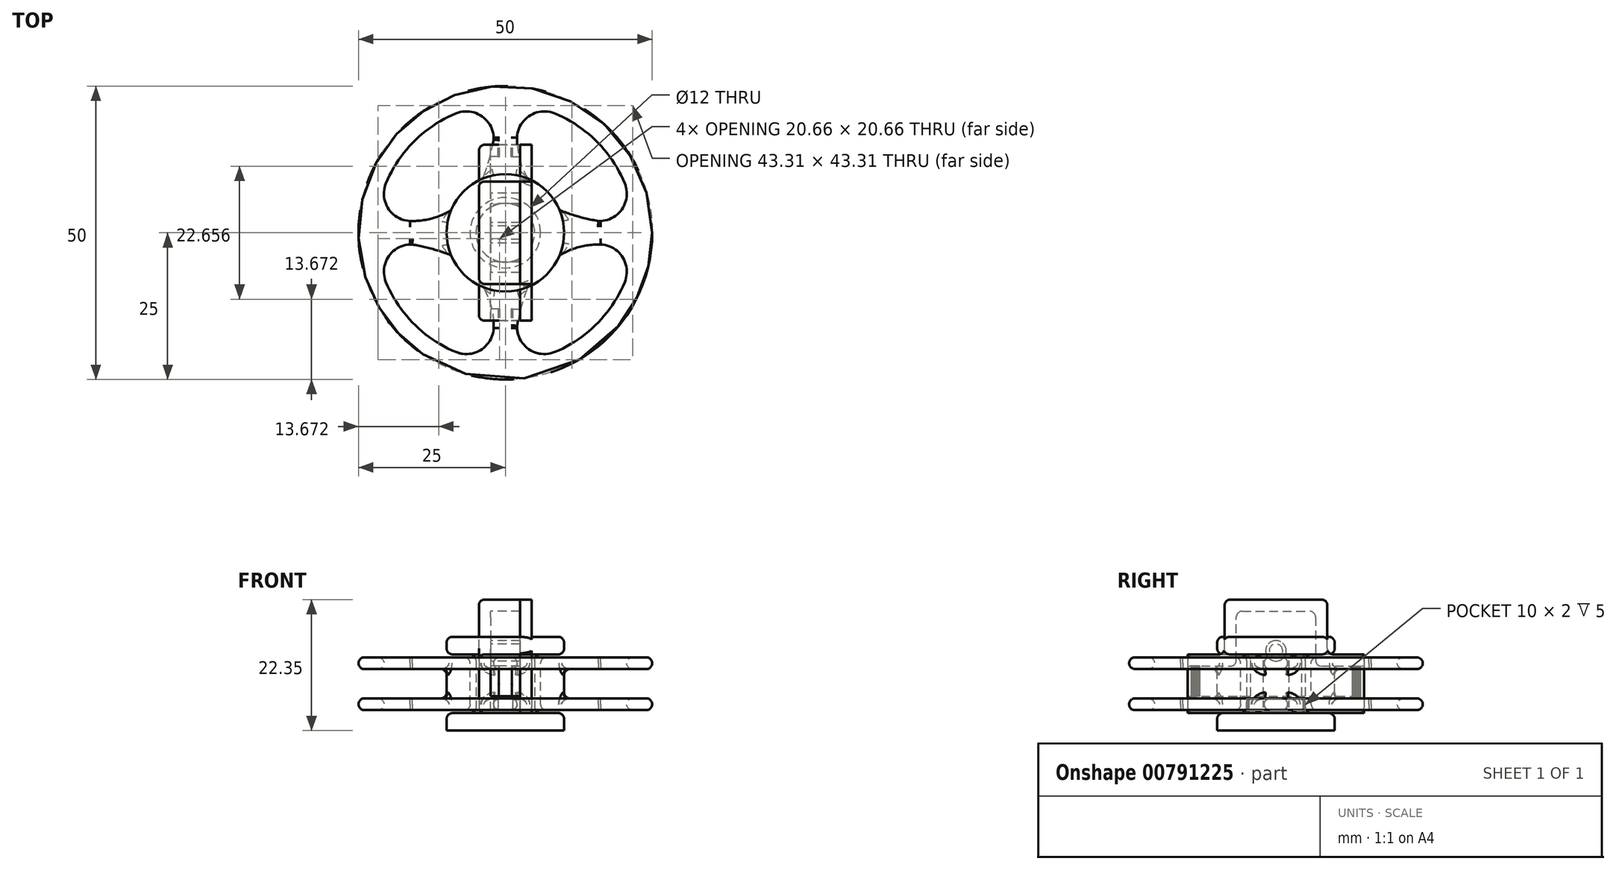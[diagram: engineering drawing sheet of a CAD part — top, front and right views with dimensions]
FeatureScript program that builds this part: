
annotation { "Feature Type Name" : "Feature", "Feature Type Description" : "" }
export const myFeature = defineFeature(function(context is Context, id is Id, definition is map)
    precondition{}
    {
        {
            var Q0;
            Q0=qCreatedBy(makeId("Right.planeOp"),FACE);
            var sketch = newSketch(context, id + "F0", { "sketchPlane" : qUnion([Q0])});
            skPoint(sketch, "E0.middle", {"position": v(0, 0) * mm});
            skLineSegment(sketch, "E1.top", {"start": v(0, 4.5) * mm, "end": v(25, 4.5) * mm});
            skLineSegment(sketch, "E1.right", {"start": v(25, 2.5) * mm, "end": v(25, 4.5) * mm});
            skLineSegment(sketch, "E2.top", {"start": v(0, -4.5) * mm, "end": v(25, -4.5) * mm});
            skLineSegment(sketch, "E2.right", {"start": v(25, -2.5) * mm, "end": v(25, -4.5) * mm});
            skLineSegment(sketch, "E3", {"start": v(10, 2.5) * mm, "end": v(25, 2.5) * mm});
            skLineSegment(sketch, "E4", {"start": v(10, -2.5) * mm, "end": v(25, -2.5) * mm});
            skLineSegment(sketch, "E5", {"start": v(0, 4.5) * mm, "end": v(0, -4.5) * mm});
            skLineSegment(sketch, "E6", {"start": v(10, 2.5) * mm, "end": v(10, -2.5) * mm});
            skSolve(sketch);
        }
        {
            var Q0;
            Q0=makeQuery(id+"F0.imprint","IMPRINT",FACE,{"disambiguationData":[TD([[makeQuery(id+"F0.imprint","IMPRINT",EDGE,{"derivedFrom":sQuery(id+"F0.wireOp",EDGE,"E1.top")}),-1.0]])]});
            var Q1;
            Q1=sQuery(id+"F0.wireOp",EDGE,"E5");
            revolve(context, id + "F1", {"surfaceOperationType" : NewSurfaceOperationType.NEW, "entities" : qUnion([Q0]), "axis" : qUnion([Q1]), "revolveType" : RevolveType.FULL});
        }
        {
            var Q0;
            Q0=makeQuery(id+"F1.opRevolve","SWEPT_FACE",FACE,{"disambiguationData":[OSD([sQuery(id+"F0.wireOp",EDGE,"E1.top")])]});
            var sketch = newSketch(context, id + "F2", { "sketchPlane" : qUnion([Q0])});
            skCircle(sketch, "E7", {"center": v(0, 0) * mm, "radius": 6 * mm});
            skCircle(sketch, "E8", {"center": v(0, 0) * mm, "radius": 10 * mm});
            skCircle(sketch, "E9", {"center": v(0, 0) * mm, "radius": 22 * mm});
            skLineSegment(sketch, "E10", {"start": v(-2, 9.8) * mm, "end": v(-2, 21.9) * mm});
            skLineSegment(sketch, "E11", {"start": v(2, 9.8) * mm, "end": v(2, 21.9) * mm});
            skLineSegment(sketch, "E12.1.0", {"start": v(-9.8, -2) * mm, "end": v(-21.9, -2) * mm});
            skLineSegment(sketch, "E12.1.1", {"start": v(-9.8, 2) * mm, "end": v(-21.9, 2) * mm});
            skLineSegment(sketch, "E12.2.0", {"start": v(2, -9.8) * mm, "end": v(2, -21.9) * mm});
            skLineSegment(sketch, "E12.2.1", {"start": v(-2, -9.8) * mm, "end": v(-2, -21.9) * mm});
            skLineSegment(sketch, "E12.3.0", {"start": v(9.8, 2) * mm, "end": v(21.9, 2) * mm});
            skLineSegment(sketch, "E12.3.1", {"start": v(9.8, -2) * mm, "end": v(21.9, -2) * mm});
            skArc(sketch, "E13", {"start": v(-15.85, 2) * mm, "mid": v(-12.42, 2.47) * mm, "end": v(-9.24, 3.83) * mm});
            skArc(sketch, "E14", {"start": v(-3.83, 9.24) * mm, "mid": v(-2.74, 12.5) * mm, "end": v(-2, 15.85) * mm});
            skArc(sketch, "E15", {"start": v(-20.33, 8.42) * mm, "mid": v(-19.85, 3.99) * mm, "end": v(-15.85, 2) * mm});
            skArc(sketch, "E16", {"start": v(-2, 15.85) * mm, "mid": v(-3.99, 19.85) * mm, "end": v(-8.42, 20.33) * mm});
            skArc(sketch, "E17.1.0", {"start": v(-9.24, -3.83) * mm, "mid": v(-12.5, -2.74) * mm, "end": v(-15.85, -2) * mm});
            skArc(sketch, "E17.1.1", {"start": v(-15.85, -2) * mm, "mid": v(-19.85, -3.99) * mm, "end": v(-20.33, -8.42) * mm});
            skArc(sketch, "E17.1.2", {"start": v(-8.42, -20.33) * mm, "mid": v(-3.99, -19.85) * mm, "end": v(-2, -15.85) * mm});
            skArc(sketch, "E17.1.3", {"start": v(-2, -15.85) * mm, "mid": v(-2.47, -12.42) * mm, "end": v(-3.83, -9.24) * mm});
            skArc(sketch, "E17.2.0", {"start": v(3.83, -9.24) * mm, "mid": v(2.74, -12.5) * mm, "end": v(2, -15.85) * mm});
            skArc(sketch, "E17.2.1", {"start": v(2, -15.85) * mm, "mid": v(3.99, -19.85) * mm, "end": v(8.42, -20.33) * mm});
            skArc(sketch, "E17.2.2", {"start": v(20.33, -8.42) * mm, "mid": v(19.85, -3.99) * mm, "end": v(15.85, -2) * mm});
            skArc(sketch, "E17.2.3", {"start": v(15.85, -2) * mm, "mid": v(12.42, -2.47) * mm, "end": v(9.24, -3.83) * mm});
            skArc(sketch, "E17.3.0", {"start": v(9.24, 3.83) * mm, "mid": v(12.5, 2.74) * mm, "end": v(15.85, 2) * mm});
            skArc(sketch, "E17.3.1", {"start": v(15.85, 2) * mm, "mid": v(19.85, 3.99) * mm, "end": v(20.33, 8.42) * mm});
            skArc(sketch, "E17.3.2", {"start": v(8.42, 20.33) * mm, "mid": v(3.99, 19.85) * mm, "end": v(2, 15.85) * mm});
            skArc(sketch, "E17.3.3", {"start": v(2, 15.85) * mm, "mid": v(2.47, 12.42) * mm, "end": v(3.83, 9.24) * mm});
            skSolve(sketch);
        }
        {
            var Q0;
            {var subQ1=sQuery(id+"F2.wireOp",EDGE,"E13");Q0=makeQuery(id+"F2.imprint","IMPRINT",FACE,{"disambiguationData":[TD([[makeQuery(id+"F2.imprint","IMPRINT",EDGE,{"derivedFrom":subQ1}),1.0]])]});}
            var Q1;
            {var subQ8=sQuery(id+"F2.wireOp",EDGE,"E17.1.0");Q1=makeQuery(id+"F2.imprint","IMPRINT",FACE,{"disambiguationData":[TD([[makeQuery(id+"F2.imprint","IMPRINT",EDGE,{"derivedFrom":subQ8}),1.0]])]});}
            var Q2;
            {var subQ1=sQuery(id+"F2.wireOp",EDGE,"E17.2.0");Q2=makeQuery(id+"F2.imprint","IMPRINT",FACE,{"disambiguationData":[TD([[makeQuery(id+"F2.imprint","IMPRINT",EDGE,{"derivedFrom":subQ1}),1.0]])]});}
            var Q3;
            {var subQ5=sQuery(id+"F2.wireOp",EDGE,"E17.3.0");Q3=makeQuery(id+"F2.imprint","IMPRINT",FACE,{"disambiguationData":[TD([[makeQuery(id+"F2.imprint","IMPRINT",EDGE,{"derivedFrom":subQ5}),1.0]])]});}
            var Q4;
            Q4=makeQuery(id+"F2.imprint","IMPRINT",FACE,{"disambiguationData":[TD([[makeQuery(id+"F2.imprint","IMPRINT",EDGE,{"derivedFrom":sQuery(id+"F2.wireOp",EDGE,"E7")}),1.0]])]});
            extrude(context, id + "F3", {"entities" : qUnion([Q0, Q1, Q2, Q3, Q4]), "operationType" : NewBodyOperationType.REMOVE, "oppositeDirection" : true, "depth" : 25 * mm, "offsetDistance" : 25 * mm});
        }
        {
            var Q0;
            Q0=makeQuery(id+"F1.opRevolve","SWEPT_FACE",FACE,{"disambiguationData":[OSD([sQuery(id+"F0.wireOp",EDGE,"E1.top")])]});
            var Q1;
            Q1=makeQuery(id+"F1.opRevolve","SWEPT_FACE",FACE,{"disambiguationData":[OSD([sQuery(id+"F0.wireOp",EDGE,"E2.top")])]});
            var Q2;
            Q2=makeQuery(id+"F1.opRevolve","SWEPT_FACE",FACE,{"disambiguationData":[OSD([sQuery(id+"F0.wireOp",EDGE,"E3")])]});
            var Q3;
            Q3=makeQuery(id+"F1.opRevolve","SWEPT_FACE",FACE,{"disambiguationData":[OSD([sQuery(id+"F0.wireOp",EDGE,"E4")])]});
            var Q4;
            {var subQ0=sQuery(id+"F2.wireOp",EDGE,"E8");Q4=makeQuery(id+"F3.boolean.opBoolean","MERGE",FACE,{"derivedFrom":[makeQuery(id+"F1.opRevolve","SWEPT_FACE",FACE,{"disambiguationData":[OSD([sQuery(id+"F0.wireOp",EDGE,"E6")])]}),makeQuery(id+"F3.opExtrude","SWEPT_FACE",FACE,{"disambiguationData":[OSD([subQ0]),TDD([makeQuery(id+"F2.imprint","IMPRINT",EDGE,{"disambiguationData":[TD([[makeQuery(id+"F2.imprint","INTERSECT",VERTEX,{"derivedFrom":[subQ0,sQuery(id+"F2.wireOp",EDGE,"E17.3.0")]}),-1.0]])],"derivedFrom":subQ0})])]}),makeQuery(id+"F3.opExtrude","SWEPT_FACE",FACE,{"disambiguationData":[OSD([subQ0]),TDD([makeQuery(id+"F2.imprint","IMPRINT",EDGE,{"disambiguationData":[TD([[makeQuery(id+"F2.imprint","INTERSECT",VERTEX,{"derivedFrom":[subQ0,sQuery(id+"F2.wireOp",EDGE,"E13")]}),1.0]])],"derivedFrom":subQ0})])]}),makeQuery(id+"F3.opExtrude","SWEPT_FACE",FACE,{"disambiguationData":[OSD([subQ0]),TDD([makeQuery(id+"F2.imprint","IMPRINT",EDGE,{"disambiguationData":[TD([[makeQuery(id+"F2.imprint","INTERSECT",VERTEX,{"derivedFrom":[subQ0,sQuery(id+"F2.wireOp",EDGE,"E17.1.0")]}),-1.0]])],"derivedFrom":subQ0})])]}),makeQuery(id+"F3.opExtrude","SWEPT_FACE",FACE,{"disambiguationData":[OSD([subQ0]),TDD([makeQuery(id+"F2.imprint","IMPRINT",EDGE,{"disambiguationData":[TD([[makeQuery(id+"F2.imprint","INTERSECT",VERTEX,{"derivedFrom":[subQ0,sQuery(id+"F2.wireOp",EDGE,"E17.2.0")]}),-1.0]])],"derivedFrom":subQ0})])]})]});}
            fillet(context, id + "F4", {"entities" : qUnion([Q0, Q1, Q2, Q3, Q4]), "radius" : 1 * mm, "tangentPropagation" : true, "allowEdgeOverflow" : false});
        }
        {
            var Q0;
            Q0=qCreatedBy(makeId("Right.planeOp"),FACE);
            var sketch = newSketch(context, id + "F5", { "sketchPlane" : qUnion([Q0])});
            skLineSegment(sketch, "E18.bottom", {"start": v(0, -5) * mm, "end": v(5, -5) * mm});
            skLineSegment(sketch, "E18.left", {"start": v(0, -5) * mm, "end": v(0, 0) * mm});
            skLineSegment(sketch, "E18.right", {"start": v(5, -5) * mm, "end": v(5, 0) * mm});
            skLineSegment(sketch, "E19.bottom", {"start": v(0, -5) * mm, "end": v(10, -5) * mm});
            skLineSegment(sketch, "E19.top", {"start": v(0, -8) * mm, "end": v(10, -8) * mm});
            skLineSegment(sketch, "E19.left", {"start": v(0, -5) * mm, "end": v(0, -8) * mm});
            skLineSegment(sketch, "E19.right", {"start": v(10, -5) * mm, "end": v(10, -8) * mm});
            skPoint(sketch, "E20", {"position": v(0, 0) * mm});
            skLineSegment(sketch, "E21", {"start": v(0, 0) * mm, "end": v(5, 0) * mm});
            skLineSegment(sketch, "E22.MirrorCS", {"start": v(0, 5) * mm, "end": v(0, 0) * mm});
            skLineSegment(sketch, "E23.MirrorCS", {"start": v(0, 8) * mm, "end": v(10, 8) * mm});
            skLineSegment(sketch, "E24.MirrorCS", {"start": v(10, 5) * mm, "end": v(10, 8) * mm});
            skLineSegment(sketch, "E25.MirrorCS", {"start": v(0, 5) * mm, "end": v(10, 5) * mm});
            skLineSegment(sketch, "E26.MirrorCS", {"start": v(5, 5) * mm, "end": v(5, 0) * mm});
            skLineSegment(sketch, "E27.MirrorCS", {"start": v(0, 5) * mm, "end": v(0, 8) * mm});
            skSolve(sketch);
        }
        {
            var Q0;
            Q0 = qSketchRegion(id + "F5", true);
            var Q1;
            Q1=sQuery(id+"F5.wireOp",EDGE,"E18.left");
            revolve(context, id + "F6", {"surfaceOperationType" : NewSurfaceOperationType.NEW, "entities" : qUnion([Q0]), "axis" : qUnion([Q1]), "revolveType" : RevolveType.FULL});
        }
        {
            var Q0;
            Q0=makeQuery(id+"F6.opRevolve","SWEPT_FACE",FACE,{"disambiguationData":[OSD([sQuery(id+"F5.wireOp",EDGE,"E23.MirrorCS")])]});
            var Q1;
            Q1=makeQuery(id+"F6.opRevolve","SWEPT_FACE",FACE,{"disambiguationData":[OSD([sQuery(id+"F5.wireOp",EDGE,"E19.bottom")])]});
            var Q2;
            Q2=makeQuery(id+"F6.opRevolve","SWEPT_FACE",FACE,{"disambiguationData":[OSD([sQuery(id+"F5.wireOp",EDGE,"E25.MirrorCS")])]});
            fillet(context, id + "F7", {"entities" : qUnion([Q0, Q1, Q2]), "radius" : 1 * mm, "tangentPropagation" : true, "allowEdgeOverflow" : false});
        }
        {
            var Q0;
            Q0=qCreatedBy(makeId("Right.planeOp"),FACE);
            var sketch = newSketch(context, id + "F8", { "sketchPlane" : qUnion([Q0])});
            skLineSegment(sketch, "E28.bottom", {"start": v(15, 5) * mm, "end": v(9.75, 5) * mm});
            skLineSegment(sketch, "E28.top", {"start": v(15, -5) * mm, "end": v(-15, -5) * mm});
            skLineSegment(sketch, "E28.left", {"start": v(15, 5) * mm, "end": v(15, -5) * mm});
            skLineSegment(sketch, "E28.right", {"start": v(-15, 5) * mm, "end": v(-15, -5) * mm});
            skPoint(sketch, "E28.middle", {"position": v(0, 0) * mm});
            skLineSegment(sketch, "E29", {"start": v(-15, -2.14) * mm, "end": v(15, -2.14) * mm});
            skLineSegment(sketch, "E30", {"start": v(-15, 3) * mm, "end": v(-9.43, 3) * mm});
            skLineSegment(sketch, "E31.top", {"start": v(-7.75, 14.35) * mm, "end": v(7.75, 14.35) * mm});
            skPoint(sketch, "E32", {"position": v(0, 14.35) * mm});
            skLineSegment(sketch, "E33", {"start": v(-8.75, 6) * mm, "end": v(-8.75, 13.35) * mm});
            skLineSegment(sketch, "E34", {"start": v(-9.75, 5) * mm, "end": v(-15, 5) * mm});
            skLineSegment(sketch, "E35", {"start": v(8.75, 6) * mm, "end": v(8.75, 13.35) * mm});
            skLineSegment(sketch, "E36", {"start": v(7.75, 3) * mm, "end": v(15, 3) * mm});
            skLineSegment(sketch, "E37", {"start": v(-9.43, 3) * mm, "end": v(-7.75, 3) * mm});
            skLineSegment(sketch, "E38", {"start": v(-6.75, 4) * mm, "end": v(-6.75, 11.35) * mm});
            skLineSegment(sketch, "E39", {"start": v(-5.75, 12.35) * mm, "end": v(5.75, 12.35) * mm});
            skLineSegment(sketch, "E40", {"start": v(6.75, 11.35) * mm, "end": v(6.75, 4) * mm});
            skPoint(sketch, "E41.visualSharp", {"position": v(-6.75, 3) * mm});
            skArc(sketch, "E41.filletArc", {"start": v(-7.75, 3) * mm, "mid": v(-7.04, 3.3) * mm, "end": v(-6.75, 4) * mm});
            skPoint(sketch, "E42.visualSharp", {"position": v(-6.75, 12.35) * mm});
            skArc(sketch, "E42.filletArc", {"start": v(-5.75, 12.35) * mm, "mid": v(-6.45, 12.06) * mm, "end": v(-6.75, 11.35) * mm});
            skPoint(sketch, "E43.visualSharp", {"position": v(6.75, 12.35) * mm});
            skArc(sketch, "E43.filletArc", {"start": v(6.75, 11.35) * mm, "mid": v(6.45, 12.06) * mm, "end": v(5.75, 12.35) * mm});
            skPoint(sketch, "E44.visualSharp", {"position": v(6.75, 3) * mm});
            skArc(sketch, "E44.filletArc", {"start": v(6.75, 4) * mm, "mid": v(7.04, 3.3) * mm, "end": v(7.75, 3) * mm});
            skPoint(sketch, "E45.visualSharp", {"position": v(-8.75, 5) * mm});
            skArc(sketch, "E45.filletArc", {"start": v(-9.75, 5) * mm, "mid": v(-9.04, 5.3) * mm, "end": v(-8.75, 6) * mm});
            skPoint(sketch, "E46.visualSharp", {"position": v(-8.75, 14.35) * mm});
            skArc(sketch, "E46.filletArc", {"start": v(-7.75, 14.35) * mm, "mid": v(-8.45, 14.06) * mm, "end": v(-8.75, 13.35) * mm});
            skPoint(sketch, "E47.visualSharp", {"position": v(8.75, 14.35) * mm});
            skArc(sketch, "E47.filletArc", {"start": v(8.75, 13.35) * mm, "mid": v(8.45, 14.06) * mm, "end": v(7.75, 14.35) * mm});
            skPoint(sketch, "E48.visualSharp", {"position": v(8.75, 5) * mm});
            skArc(sketch, "E48.filletArc", {"start": v(8.75, 6) * mm, "mid": v(9.04, 5.3) * mm, "end": v(9.75, 5) * mm});
            skCircle(sketch, "E49", {"center": v(0, 5.6) * mm, "radius": 1.75 * mm});
            skCircle(sketch, "E50", {"center": v(0, 5.6) * mm, "radius": 1.15 * mm});
            skLineSegment(sketch, "E51", {"start": v(-8.45, 14.06) * mm, "end": v(-6.45, 12.06) * mm, "construction": true});
            skLineSegment(sketch, "E52", {"start": v(6.45, 12.06) * mm, "end": v(8.45, 14.06) * mm, "construction": true});
            skLineSegment(sketch, "E53", {"start": v(7.04, 3.3) * mm, "end": v(9.04, 5.3) * mm, "construction": true});
            skLineSegment(sketch, "E54", {"start": v(-9.04, 5.3) * mm, "end": v(-7.04, 3.3) * mm, "construction": true});
            skLineSegment(sketch, "E55.bottom", {"start": v(5, -4.56) * mm, "end": v(-5, -4.56) * mm});
            skLineSegment(sketch, "E55.top", {"start": v(5, -2.56) * mm, "end": v(-5, -2.56) * mm});
            skLineSegment(sketch, "E55.left", {"start": v(5, -4.56) * mm, "end": v(5, -2.56) * mm});
            skLineSegment(sketch, "E55.right", {"start": v(-5, -4.56) * mm, "end": v(-5, -2.56) * mm});
            skPoint(sketch, "E55.middle", {"position": v(0, -3.56) * mm});
            skPoint(sketch, "E55.middle.positionSnap0", {"position": v(0, -5) * mm});
            skPoint(sketch, "E55.centerSnap0", {"position": v(0, -5) * mm});
            skSolve(sketch);
        }
        {
            var Q0;
            {var subQ2=sQuery(id+"F8.wireOp",EDGE,"E28.bottom");Q0=makeQuery(id+"F8.imprint","IMPRINT",FACE,{"disambiguationData":[TD([[makeQuery(id+"F8.imprint","IMPRINT",EDGE,{"derivedFrom":subQ2}),1.0]])]});}
            var Q1;
            Q1=makeQuery(id+"F8.imprint","IMPRINT",FACE,{"disambiguationData":[TD([[makeQuery(id+"F8.imprint","IMPRINT",EDGE,{"derivedFrom":sQuery(id+"F8.wireOp",EDGE,"E49")}),1.0]])]});
            var Q2;
            {var subQ0=sQuery(id+"F8.wireOp",EDGE,"E28.top");Q2=makeQuery(id+"F8.imprint","IMPRINT",FACE,{"disambiguationData":[TD([[makeQuery(id+"F8.imprint","IMPRINT",EDGE,{"derivedFrom":subQ0}),-1.0]])]});}
            extrude(context, id + "F9", {"entities" : qUnion([Q0, Q1, Q2]), "endBound" : BoundingType.SYMMETRIC, "depth" : 5 * mm, "offsetDistance" : 25 * mm});
        }
        {
            var Q0;
            Q0=makeQuery(id+"F9.opExtrude","CAP_FACE",FACE,{"disambiguationData":[OSD([sQuery(id+"F8.wireOp",EDGE,"E49")])],"isStart":true});
            var sketch = newSketch(context, id + "F10", { "sketchPlane" : qUnion([Q0])});
            skLineSegment(sketch, "E56.bottom", {"start": v(15, 5) * mm, "end": v(9.75, 5) * mm});
            skLineSegment(sketch, "E56.top", {"start": v(15, -5) * mm, "end": v(-15, -5) * mm});
            skLineSegment(sketch, "E56.left", {"start": v(15, 5) * mm, "end": v(15, -5) * mm});
            skLineSegment(sketch, "E56.right", {"start": v(-15, 5) * mm, "end": v(-15, -5) * mm});
            skPoint(sketch, "E56.middle", {"position": v(0, 0) * mm});
            skLineSegment(sketch, "E57", {"start": v(-15, -2.14) * mm, "end": v(15, -2.14) * mm});
            skLineSegment(sketch, "E58", {"start": v(-15, 3) * mm, "end": v(-9.43, 3) * mm});
            skLineSegment(sketch, "E59.top", {"start": v(-7.75, 14.35) * mm, "end": v(7.75, 14.35) * mm});
            skPoint(sketch, "E60", {"position": v(0, 14.35) * mm});
            skLineSegment(sketch, "E61", {"start": v(-8.75, 6) * mm, "end": v(-8.75, 13.35) * mm});
            skLineSegment(sketch, "E62", {"start": v(-9.75, 5) * mm, "end": v(-15, 5) * mm});
            skLineSegment(sketch, "E63", {"start": v(8.75, 6) * mm, "end": v(8.75, 13.35) * mm});
            skLineSegment(sketch, "E64", {"start": v(7.75, 3) * mm, "end": v(15, 3) * mm});
            skLineSegment(sketch, "E65", {"start": v(-9.43, 3) * mm, "end": v(-7.75, 3) * mm});
            skLineSegment(sketch, "E66", {"start": v(-6.75, 4) * mm, "end": v(-6.75, 11.35) * mm});
            skLineSegment(sketch, "E67", {"start": v(-5.75, 12.35) * mm, "end": v(5.75, 12.35) * mm});
            skLineSegment(sketch, "E68", {"start": v(6.75, 11.35) * mm, "end": v(6.75, 4) * mm});
            skPoint(sketch, "E69.visualSharp", {"position": v(-6.75, 3) * mm});
            skArc(sketch, "E69.filletArc", {"start": v(-7.75, 3) * mm, "mid": v(-7.04, 3.3) * mm, "end": v(-6.75, 4) * mm});
            skPoint(sketch, "E70.visualSharp", {"position": v(-6.75, 12.35) * mm});
            skArc(sketch, "E70.filletArc", {"start": v(-5.75, 12.35) * mm, "mid": v(-6.45, 12.06) * mm, "end": v(-6.75, 11.35) * mm});
            skPoint(sketch, "E71.visualSharp", {"position": v(6.75, 12.35) * mm});
            skArc(sketch, "E71.filletArc", {"start": v(6.75, 11.35) * mm, "mid": v(6.45, 12.06) * mm, "end": v(5.75, 12.35) * mm});
            skPoint(sketch, "E72.visualSharp", {"position": v(6.75, 3) * mm});
            skArc(sketch, "E72.filletArc", {"start": v(6.75, 4) * mm, "mid": v(7.04, 3.3) * mm, "end": v(7.75, 3) * mm});
            skPoint(sketch, "E73.visualSharp", {"position": v(-8.75, 5) * mm});
            skArc(sketch, "E73.filletArc", {"start": v(-9.75, 5) * mm, "mid": v(-9.04, 5.3) * mm, "end": v(-8.75, 6) * mm});
            skPoint(sketch, "E74.visualSharp", {"position": v(-8.75, 14.35) * mm});
            skArc(sketch, "E74.filletArc", {"start": v(-7.75, 14.35) * mm, "mid": v(-8.45, 14.06) * mm, "end": v(-8.75, 13.35) * mm});
            skPoint(sketch, "E75.visualSharp", {"position": v(8.75, 14.35) * mm});
            skArc(sketch, "E75.filletArc", {"start": v(8.75, 13.35) * mm, "mid": v(8.45, 14.06) * mm, "end": v(7.75, 14.35) * mm});
            skPoint(sketch, "E76.visualSharp", {"position": v(8.75, 5) * mm});
            skArc(sketch, "E76.filletArc", {"start": v(8.75, 6) * mm, "mid": v(9.04, 5.3) * mm, "end": v(9.75, 5) * mm});
            skCircle(sketch, "E77", {"center": v(0, 5.6) * mm, "radius": 1.75 * mm});
            skSolve(sketch);
        }
        {
            var Q0;
            Q0 = qSketchRegion(id + "F10", true);
            var Q1;
            Q1=makeQuery(id+"F10.imprint","IMPRINT",FACE,{"disambiguationData":[TD([[makeQuery(id+"F10.imprint","IMPRINT",EDGE,{"derivedFrom":sQuery(id+"F10.wireOp",EDGE,"E77")}),-1.0]])]});
            var Q2;
            Q2=makeQuery(id+"F10.imprint","IMPRINT",FACE,{"disambiguationData":[TD([[makeQuery(id+"F10.imprint","IMPRINT",EDGE,{"derivedFrom":makeQuery(id+"F9.opExtrude","CAP_EDGE",EDGE,{"disambiguationData":[OSD([sQuery(id+"F8.wireOp",EDGE,"E50")])],"isStart":true})}),-1.0]])]});
            extrude(context, id + "F11", {"entities" : qUnion([Q0, Q1, Q2]), "depth" : 2 * mm, "offsetDistance" : 25 * mm});
        }
        {
            var Q0;
            Q0=makeQuery(id+"F9.opExtrude","CAP_FACE",FACE,{"disambiguationData":[OSD([sQuery(id+"F8.wireOp",EDGE,"E28.bottom"),sQuery(id+"F8.wireOp",EDGE,"E28.left"),sQuery(id+"F8.wireOp",EDGE,"E28.right"),sQuery(id+"F8.wireOp",EDGE,"E30"),sQuery(id+"F8.wireOp",EDGE,"E31.top"),sQuery(id+"F8.wireOp",EDGE,"E33"),sQuery(id+"F8.wireOp",EDGE,"E34"),sQuery(id+"F8.wireOp",EDGE,"E35"),sQuery(id+"F8.wireOp",EDGE,"E36"),sQuery(id+"F8.wireOp",EDGE,"E37"),sQuery(id+"F8.wireOp",EDGE,"E38"),sQuery(id+"F8.wireOp",EDGE,"E39"),sQuery(id+"F8.wireOp",EDGE,"E40"),sQuery(id+"F8.wireOp",EDGE,"E41.filletArc"),sQuery(id+"F8.wireOp",EDGE,"E42.filletArc"),sQuery(id+"F8.wireOp",EDGE,"E43.filletArc"),sQuery(id+"F8.wireOp",EDGE,"E44.filletArc"),sQuery(id+"F8.wireOp",EDGE,"E45.filletArc"),sQuery(id+"F8.wireOp",EDGE,"E46.filletArc"),sQuery(id+"F8.wireOp",EDGE,"E47.filletArc"),sQuery(id+"F8.wireOp",EDGE,"E48.filletArc")])],"isStart":false});
            var sketch = newSketch(context, id + "F12", { "sketchPlane" : qUnion([Q0])});
            skLineSegment(sketch, "E78.bottom", {"start": v(15, 5) * mm, "end": v(9.75, 5) * mm});
            skLineSegment(sketch, "E78.top", {"start": v(15, -5) * mm, "end": v(-15, -5) * mm});
            skLineSegment(sketch, "E78.left", {"start": v(15, 5) * mm, "end": v(15, -5) * mm});
            skLineSegment(sketch, "E78.right", {"start": v(-15, 5) * mm, "end": v(-15, -5) * mm});
            skPoint(sketch, "E78.middle", {"position": v(0, 0) * mm});
            skLineSegment(sketch, "E79", {"start": v(-15, -2.14) * mm, "end": v(15, -2.14) * mm});
            skLineSegment(sketch, "E80", {"start": v(-15, 3) * mm, "end": v(-9.43, 3) * mm});
            skLineSegment(sketch, "E81.top", {"start": v(-7.75, 14.35) * mm, "end": v(7.75, 14.35) * mm});
            skPoint(sketch, "E82", {"position": v(0, 14.35) * mm});
            skLineSegment(sketch, "E83", {"start": v(-8.75, 6) * mm, "end": v(-8.75, 13.35) * mm});
            skLineSegment(sketch, "E84", {"start": v(-9.75, 5) * mm, "end": v(-15, 5) * mm});
            skLineSegment(sketch, "E85", {"start": v(8.75, 6) * mm, "end": v(8.75, 13.35) * mm});
            skLineSegment(sketch, "E86", {"start": v(7.75, 3) * mm, "end": v(15, 3) * mm});
            skLineSegment(sketch, "E87", {"start": v(-9.43, 3) * mm, "end": v(-7.75, 3) * mm});
            skLineSegment(sketch, "E88", {"start": v(-6.75, 4) * mm, "end": v(-6.75, 11.35) * mm});
            skLineSegment(sketch, "E89", {"start": v(-5.75, 12.35) * mm, "end": v(5.75, 12.35) * mm});
            skLineSegment(sketch, "E90", {"start": v(6.75, 11.35) * mm, "end": v(6.75, 4) * mm});
            skPoint(sketch, "E91.visualSharp", {"position": v(-6.75, 3) * mm});
            skArc(sketch, "E91.filletArc", {"start": v(-7.75, 3) * mm, "mid": v(-7.04, 3.3) * mm, "end": v(-6.75, 4) * mm});
            skPoint(sketch, "E92.visualSharp", {"position": v(-6.75, 12.35) * mm});
            skArc(sketch, "E92.filletArc", {"start": v(-5.75, 12.35) * mm, "mid": v(-6.45, 12.06) * mm, "end": v(-6.75, 11.35) * mm});
            skPoint(sketch, "E93.visualSharp", {"position": v(6.75, 12.35) * mm});
            skArc(sketch, "E93.filletArc", {"start": v(6.75, 11.35) * mm, "mid": v(6.45, 12.06) * mm, "end": v(5.75, 12.35) * mm});
            skPoint(sketch, "E94.visualSharp", {"position": v(6.75, 3) * mm});
            skArc(sketch, "E94.filletArc", {"start": v(6.75, 4) * mm, "mid": v(7.04, 3.3) * mm, "end": v(7.75, 3) * mm});
            skPoint(sketch, "E95.visualSharp", {"position": v(-8.75, 5) * mm});
            skArc(sketch, "E95.filletArc", {"start": v(-9.75, 5) * mm, "mid": v(-9.04, 5.3) * mm, "end": v(-8.75, 6) * mm});
            skPoint(sketch, "E96.visualSharp", {"position": v(-8.75, 14.35) * mm});
            skArc(sketch, "E96.filletArc", {"start": v(-7.75, 14.35) * mm, "mid": v(-8.45, 14.06) * mm, "end": v(-8.75, 13.35) * mm});
            skPoint(sketch, "E97.visualSharp", {"position": v(8.75, 14.35) * mm});
            skArc(sketch, "E97.filletArc", {"start": v(8.75, 13.35) * mm, "mid": v(8.45, 14.06) * mm, "end": v(7.75, 14.35) * mm});
            skPoint(sketch, "E98.visualSharp", {"position": v(8.75, 5) * mm});
            skArc(sketch, "E98.filletArc", {"start": v(8.75, 6) * mm, "mid": v(9.04, 5.3) * mm, "end": v(9.75, 5) * mm});
            skCircle(sketch, "E99", {"center": v(0, 5.6) * mm, "radius": 1.75 * mm});
            skSolve(sketch);
        }
        {
            var Q0;
            Q0 = qSketchRegion(id + "F12", true);
            var Q1;
            Q1=makeQuery(id+"F12.imprint","IMPRINT",FACE,{"disambiguationData":[TD([[makeQuery(id+"F12.imprint","IMPRINT",EDGE,{"derivedFrom":sQuery(id+"F12.wireOp",EDGE,"E99")}),1.0]])]});
            extrude(context, id + "F13", {"entities" : qUnion([Q0, Q1]), "depth" : 2 * mm, "offsetDistance" : 25 * mm});
        }
        {
            var Q0;
            Q0=makeQuery(id+"F11.opExtrude","SWEPT_BODY",BODY,{"disambiguationData":[OSD([sQuery(id+"F10.wireOp",EDGE,"E56.bottom"),sQuery(id+"F10.wireOp",EDGE,"E56.top"),sQuery(id+"F10.wireOp",EDGE,"E56.left"),sQuery(id+"F10.wireOp",EDGE,"E56.right"),sQuery(id+"F10.wireOp",EDGE,"E59.top"),sQuery(id+"F10.wireOp",EDGE,"E61"),sQuery(id+"F10.wireOp",EDGE,"E62"),sQuery(id+"F10.wireOp",EDGE,"E63"),sQuery(id+"F10.wireOp",EDGE,"E73.filletArc"),sQuery(id+"F10.wireOp",EDGE,"E74.filletArc"),sQuery(id+"F10.wireOp",EDGE,"E75.filletArc"),sQuery(id+"F10.wireOp",EDGE,"E76.filletArc")])]});
            var Q1;
            Q1=makeQuery(id+"F9.opExtrude","SWEPT_BODY",BODY,{"disambiguationData":[OSD([sQuery(id+"F8.wireOp",EDGE,"E28.bottom"),sQuery(id+"F8.wireOp",EDGE,"E28.left"),sQuery(id+"F8.wireOp",EDGE,"E28.right"),sQuery(id+"F8.wireOp",EDGE,"E30"),sQuery(id+"F8.wireOp",EDGE,"E31.top"),sQuery(id+"F8.wireOp",EDGE,"E33"),sQuery(id+"F8.wireOp",EDGE,"E34"),sQuery(id+"F8.wireOp",EDGE,"E35"),sQuery(id+"F8.wireOp",EDGE,"E36"),sQuery(id+"F8.wireOp",EDGE,"E37"),sQuery(id+"F8.wireOp",EDGE,"E38"),sQuery(id+"F8.wireOp",EDGE,"E39"),sQuery(id+"F8.wireOp",EDGE,"E40"),sQuery(id+"F8.wireOp",EDGE,"E41.filletArc"),sQuery(id+"F8.wireOp",EDGE,"E42.filletArc"),sQuery(id+"F8.wireOp",EDGE,"E43.filletArc"),sQuery(id+"F8.wireOp",EDGE,"E44.filletArc"),sQuery(id+"F8.wireOp",EDGE,"E45.filletArc"),sQuery(id+"F8.wireOp",EDGE,"E46.filletArc"),sQuery(id+"F8.wireOp",EDGE,"E47.filletArc"),sQuery(id+"F8.wireOp",EDGE,"E48.filletArc")])]});
            var Q2;
            Q2=makeQuery(id+"F9.opExtrude","SWEPT_BODY",BODY,{"disambiguationData":[OSD([sQuery(id+"F8.wireOp",EDGE,"E28.top"),sQuery(id+"F8.wireOp",EDGE,"E28.left"),sQuery(id+"F8.wireOp",EDGE,"E28.right"),sQuery(id+"F8.wireOp",EDGE,"E29"),sQuery(id+"F8.wireOp",EDGE,"E55.bottom"),sQuery(id+"F8.wireOp",EDGE,"E55.top"),sQuery(id+"F8.wireOp",EDGE,"E55.left"),sQuery(id+"F8.wireOp",EDGE,"E55.right")])]});
            var Q3;
            Q3=makeQuery(id+"F9.opExtrude","SWEPT_BODY",BODY,{"disambiguationData":[OSD([sQuery(id+"F8.wireOp",EDGE,"E49"),sQuery(id+"F8.wireOp",EDGE,"E50")])]});
            booleanBodies(context, id + "F14", {"operationType" : BooleanOperationType.UNION, "tools" : qUnion([Q0, Q1, Q2, Q3])});
        }
        {
            var Q0;
            Q0=makeQuery(id+"F13.opExtrude","CAP_FACE",FACE,{"disambiguationData":[OSD([sQuery(id+"F12.wireOp",EDGE,"E78.bottom"),sQuery(id+"F12.wireOp",EDGE,"E78.top"),sQuery(id+"F12.wireOp",EDGE,"E78.left"),sQuery(id+"F12.wireOp",EDGE,"E78.right"),sQuery(id+"F12.wireOp",EDGE,"E81.top"),sQuery(id+"F12.wireOp",EDGE,"E83"),sQuery(id+"F12.wireOp",EDGE,"E84"),sQuery(id+"F12.wireOp",EDGE,"E85"),sQuery(id+"F12.wireOp",EDGE,"E95.filletArc"),sQuery(id+"F12.wireOp",EDGE,"E96.filletArc"),sQuery(id+"F12.wireOp",EDGE,"E97.filletArc"),sQuery(id+"F12.wireOp",EDGE,"E98.filletArc")])],"isStart":true});
            var sketch = newSketch(context, id + "F15", { "sketchPlane" : qUnion([Q0])});
            skLineSegment(sketch, "E100.bottom", {"start": v(15, 5) * mm, "end": v(9.75, 5) * mm});
            skLineSegment(sketch, "E100.top", {"start": v(15, -5) * mm, "end": v(-15, -5) * mm});
            skLineSegment(sketch, "E100.left", {"start": v(15, 5) * mm, "end": v(15, -5) * mm});
            skLineSegment(sketch, "E100.right", {"start": v(-15, 5) * mm, "end": v(-15, -5) * mm});
            skPoint(sketch, "E100.middle", {"position": v(0, 0) * mm});
            skLineSegment(sketch, "E101", {"start": v(-15, -2.14) * mm, "end": v(15, -2.14) * mm});
            skLineSegment(sketch, "E102", {"start": v(-15, 3) * mm, "end": v(-9.43, 3) * mm});
            skLineSegment(sketch, "E103.top", {"start": v(-7.75, 14.35) * mm, "end": v(7.75, 14.35) * mm});
            skPoint(sketch, "E104", {"position": v(0, 14.35) * mm});
            skLineSegment(sketch, "E105", {"start": v(-8.75, 6) * mm, "end": v(-8.75, 13.35) * mm});
            skLineSegment(sketch, "E106", {"start": v(-9.75, 5) * mm, "end": v(-15, 5) * mm});
            skLineSegment(sketch, "E107", {"start": v(8.75, 6) * mm, "end": v(8.75, 13.35) * mm});
            skLineSegment(sketch, "E108", {"start": v(7.75, 3) * mm, "end": v(15, 3) * mm});
            skLineSegment(sketch, "E109", {"start": v(-9.43, 3) * mm, "end": v(-7.75, 3) * mm});
            skLineSegment(sketch, "E110", {"start": v(-6.75, 4) * mm, "end": v(-6.75, 11.35) * mm});
            skLineSegment(sketch, "E111", {"start": v(-5.75, 12.35) * mm, "end": v(5.75, 12.35) * mm});
            skLineSegment(sketch, "E112", {"start": v(6.75, 11.35) * mm, "end": v(6.75, 4) * mm});
            skPoint(sketch, "E113.visualSharp", {"position": v(-6.75, 3) * mm});
            skArc(sketch, "E113.filletArc", {"start": v(-7.75, 3) * mm, "mid": v(-7.04, 3.3) * mm, "end": v(-6.75, 4) * mm});
            skPoint(sketch, "E114.visualSharp", {"position": v(-6.75, 12.35) * mm});
            skArc(sketch, "E114.filletArc", {"start": v(-5.75, 12.35) * mm, "mid": v(-6.45, 12.06) * mm, "end": v(-6.75, 11.35) * mm});
            skPoint(sketch, "E115.visualSharp", {"position": v(6.75, 12.35) * mm});
            skArc(sketch, "E115.filletArc", {"start": v(6.75, 11.35) * mm, "mid": v(6.45, 12.06) * mm, "end": v(5.75, 12.35) * mm});
            skPoint(sketch, "E116.visualSharp", {"position": v(6.75, 3) * mm});
            skArc(sketch, "E116.filletArc", {"start": v(6.75, 4) * mm, "mid": v(7.04, 3.3) * mm, "end": v(7.75, 3) * mm});
            skPoint(sketch, "E117.visualSharp", {"position": v(-8.75, 5) * mm});
            skArc(sketch, "E117.filletArc", {"start": v(-9.75, 5) * mm, "mid": v(-9.04, 5.3) * mm, "end": v(-8.75, 6) * mm});
            skPoint(sketch, "E118.visualSharp", {"position": v(-8.75, 14.35) * mm});
            skArc(sketch, "E118.filletArc", {"start": v(-7.75, 14.35) * mm, "mid": v(-8.45, 14.06) * mm, "end": v(-8.75, 13.35) * mm});
            skPoint(sketch, "E119.visualSharp", {"position": v(8.75, 14.35) * mm});
            skArc(sketch, "E119.filletArc", {"start": v(8.75, 13.35) * mm, "mid": v(8.45, 14.06) * mm, "end": v(7.75, 14.35) * mm});
            skPoint(sketch, "E120.visualSharp", {"position": v(8.75, 5) * mm});
            skArc(sketch, "E120.filletArc", {"start": v(8.75, 6) * mm, "mid": v(9.04, 5.3) * mm, "end": v(9.75, 5) * mm});
            skCircle(sketch, "E121", {"center": v(0, 5.6) * mm, "radius": 1.75 * mm});
            skPoint(sketch, "E122", {"position": v(5, -2.56) * mm});
            skPoint(sketch, "E123", {"position": v(5, -4.56) * mm});
            skPoint(sketch, "E124", {"position": v(-5, -4.56) * mm});
            skPoint(sketch, "E125", {"position": v(-5, -2.56) * mm});
            skLineSegment(sketch, "E126", {"start": v(5, -2.56) * mm, "end": v(-5, -4.56) * mm, "construction": true});
            skLineSegment(sketch, "E127.bottom", {"start": v(-4.85, -2.7) * mm, "end": v(4.85, -2.7) * mm});
            skLineSegment(sketch, "E127.top", {"start": v(-4.85, -4.4) * mm, "end": v(4.85, -4.4) * mm});
            skLineSegment(sketch, "E127.left", {"start": v(-4.85, -2.7) * mm, "end": v(-4.85, -4.4) * mm});
            skLineSegment(sketch, "E127.right", {"start": v(4.85, -2.7) * mm, "end": v(4.85, -4.4) * mm});
            skPoint(sketch, "E127.middle", {"position": v(0, -3.56) * mm});
            skCircle(sketch, "E128", {"center": v(0, 5.6) * mm, "radius": 1 * mm});
            skSolve(sketch);
        }
        {
            var Q0;
            Q0=makeQuery(id+"F15.imprint","IMPRINT",FACE,{"disambiguationData":[TD([[makeQuery(id+"F15.imprint","IMPRINT",EDGE,{"derivedFrom":sQuery(id+"F15.wireOp",EDGE,"E128")}),1.0]])]});
            var Q1;
            Q1=makeQuery(id+"F15.imprint","IMPRINT",FACE,{"disambiguationData":[TD([[makeQuery(id+"F15.imprint","IMPRINT",EDGE,{"derivedFrom":sQuery(id+"F15.wireOp",EDGE,"E127.bottom")}),-1.0]])]});
            extrude(context, id + "F16", {"entities" : qUnion([Q0, Q1]), "operationType" : NewBodyOperationType.ADD, "depth" : 4.5 * mm, "offsetDistance" : 25 * mm});
        }
        {
            var Q0;
            Q0=makeQuery(id+"F13.opExtrude","SWEPT_FACE",FACE,{"disambiguationData":[OSD([sQuery(id+"F12.wireOp",EDGE,"E78.left")])]});
            var sketch = newSketch(context, id + "F17", { "sketchPlane" : qUnion([Q0])});
            skPoint(sketch, "E129", {"position": v(-2.5, 3) * mm});
            skPoint(sketch, "E130", {"position": v(-2.5, -2.14) * mm});
            skLineSegment(sketch, "E131.left", {"start": v(-2.5, 3) * mm, "end": v(-2.5, -2.1) * mm});
            skLineSegment(sketch, "E132", {"start": v(-1.25, 3) * mm, "end": v(-1, 2.88) * mm});
            skLineSegment(sketch, "E133", {"start": v(-1, 2.88) * mm, "end": v(-1.25, 2.75) * mm});
            skLineSegment(sketch, "E134.1.0.0", {"start": v(-1, 2.63) * mm, "end": v(-1.25, 2.5) * mm});
            skLineSegment(sketch, "E134.1.0.1", {"start": v(-1.25, 2.75) * mm, "end": v(-1, 2.63) * mm});
            skLineSegment(sketch, "E134.2.0.0", {"start": v(-1, 2.38) * mm, "end": v(-1.25, 2.25) * mm});
            skLineSegment(sketch, "E134.2.0.1", {"start": v(-1.25, 2.5) * mm, "end": v(-1, 2.38) * mm});
            skLineSegment(sketch, "E134.3.0.0", {"start": v(-1, 2.13) * mm, "end": v(-1.25, 2) * mm});
            skLineSegment(sketch, "E134.3.0.1", {"start": v(-1.25, 2.25) * mm, "end": v(-1, 2.13) * mm});
            skLineSegment(sketch, "E134.4.0.0", {"start": v(-1, 1.88) * mm, "end": v(-1.25, 1.75) * mm});
            skLineSegment(sketch, "E134.4.0.1", {"start": v(-1.25, 2) * mm, "end": v(-1, 1.88) * mm});
            skLineSegment(sketch, "E134.5.0.0", {"start": v(-1, 1.63) * mm, "end": v(-1.25, 1.5) * mm});
            skLineSegment(sketch, "E134.5.0.1", {"start": v(-1.25, 1.75) * mm, "end": v(-1, 1.63) * mm});
            skLineSegment(sketch, "E134.6.0.0", {"start": v(-1, 1.38) * mm, "end": v(-1.25, 1.25) * mm});
            skLineSegment(sketch, "E134.6.0.1", {"start": v(-1.25, 1.5) * mm, "end": v(-1, 1.38) * mm});
            skLineSegment(sketch, "E134.7.0.0", {"start": v(-1, 1.13) * mm, "end": v(-1.25, 1) * mm});
            skLineSegment(sketch, "E134.7.0.1", {"start": v(-1.25, 1.25) * mm, "end": v(-1, 1.13) * mm});
            skLineSegment(sketch, "E134.8.0.0", {"start": v(-1, 0.88) * mm, "end": v(-1.25, 0.75) * mm});
            skLineSegment(sketch, "E134.8.0.1", {"start": v(-1.25, 1) * mm, "end": v(-1, 0.88) * mm});
            skLineSegment(sketch, "E134.9.0.0", {"start": v(-1, 0.63) * mm, "end": v(-1.25, 0.5) * mm});
            skLineSegment(sketch, "E134.9.0.1", {"start": v(-1.25, 0.75) * mm, "end": v(-1, 0.63) * mm});
            skLineSegment(sketch, "E134.10.0.0", {"start": v(-1, 0.38) * mm, "end": v(-1.25, 0.25) * mm});
            skLineSegment(sketch, "E134.10.0.1", {"start": v(-1.25, 0.5) * mm, "end": v(-1, 0.38) * mm});
            skLineSegment(sketch, "E134.11.0.0", {"start": v(-1, 0.13) * mm, "end": v(-1.25, 0) * mm});
            skLineSegment(sketch, "E134.11.0.1", {"start": v(-1.25, 0.25) * mm, "end": v(-1, 0.13) * mm});
            skLineSegment(sketch, "E134.12.0.0", {"start": v(-1, -0.12) * mm, "end": v(-1.25, -0.25) * mm});
            skLineSegment(sketch, "E134.12.0.1", {"start": v(-1.25, 0) * mm, "end": v(-1, -0.12) * mm});
            skLineSegment(sketch, "E134.13.0.0", {"start": v(-1, -0.37) * mm, "end": v(-1.25, -0.5) * mm});
            skLineSegment(sketch, "E134.13.0.1", {"start": v(-1.25, -0.25) * mm, "end": v(-1, -0.37) * mm});
            skLineSegment(sketch, "E134.14.0.0", {"start": v(-1, -0.62) * mm, "end": v(-1.25, -0.75) * mm});
            skLineSegment(sketch, "E134.14.0.1", {"start": v(-1.25, -0.5) * mm, "end": v(-1, -0.62) * mm});
            skLineSegment(sketch, "E134.15.0.0", {"start": v(-1, -0.87) * mm, "end": v(-1.25, -1) * mm});
            skLineSegment(sketch, "E134.15.0.1", {"start": v(-1.25, -0.75) * mm, "end": v(-1, -0.87) * mm});
            skLineSegment(sketch, "E134.16.0.0", {"start": v(-1, -1.12) * mm, "end": v(-1.25, -1.25) * mm});
            skLineSegment(sketch, "E134.16.0.1", {"start": v(-1.25, -1) * mm, "end": v(-1, -1.12) * mm});
            skLineSegment(sketch, "E134.17.0.0", {"start": v(-1, -1.37) * mm, "end": v(-1.25, -1.5) * mm});
            skLineSegment(sketch, "E134.17.0.1", {"start": v(-1.25, -1.25) * mm, "end": v(-1, -1.37) * mm});
            skLineSegment(sketch, "E134.18.0.0", {"start": v(-1, -1.62) * mm, "end": v(-1.25, -1.75) * mm});
            skLineSegment(sketch, "E134.18.0.1", {"start": v(-1.25, -1.5) * mm, "end": v(-1, -1.62) * mm});
            skLineSegment(sketch, "E134.19.0.0", {"start": v(-1, -1.87) * mm, "end": v(-1.25, -2) * mm});
            skLineSegment(sketch, "E134.19.0.1", {"start": v(-1.25, -1.75) * mm, "end": v(-1, -1.87) * mm});
            skLineSegment(sketch, "E135", {"start": v(-1.25, 3) * mm, "end": v(-2.5, 3) * mm});
            skLineSegment(sketch, "E136", {"start": v(-2.5, 3) * mm, "end": v(-2.5, -2.14) * mm});
            skLineSegment(sketch, "E137", {"start": v(-1.25, -2) * mm, "end": v(-1, -2.14) * mm});
            skLineSegment(sketch, "E138", {"start": v(-1, -2.14) * mm, "end": v(-2.5, -2.14) * mm});
            skSolve(sketch);
        }
        {
            var Q0;
            Q0=makeQuery(id+"F17.imprint","IMPRINT",FACE,{"disambiguationData":[TD([[makeQuery(id+"F17.imprint","IMPRINT",EDGE,{"derivedFrom":sQuery(id+"F17.wireOp",EDGE,"E132")}),-1.0]])]});
            extrude(context, id + "F18", {"entities" : qUnion([Q0]), "oppositeDirection" : true, "depth" : 2 * mm, "offsetDistance" : 25 * mm});
        }
        {
            var Q0;
            Q0=makeQuery(id+"F18.opExtrude","SWEPT_BODY",BODY,{"disambiguationData":[OSD([sQuery(id+"F17.wireOp",EDGE,"E132"),sQuery(id+"F17.wireOp",EDGE,"E133"),sQuery(id+"F17.wireOp",EDGE,"E134.1.0.0"),sQuery(id+"F17.wireOp",EDGE,"E134.1.0.1"),sQuery(id+"F17.wireOp",EDGE,"E134.2.0.0"),sQuery(id+"F17.wireOp",EDGE,"E134.2.0.1"),sQuery(id+"F17.wireOp",EDGE,"E134.3.0.0"),sQuery(id+"F17.wireOp",EDGE,"E134.3.0.1"),sQuery(id+"F17.wireOp",EDGE,"E134.4.0.0"),sQuery(id+"F17.wireOp",EDGE,"E134.4.0.1"),sQuery(id+"F17.wireOp",EDGE,"E134.5.0.0"),sQuery(id+"F17.wireOp",EDGE,"E134.5.0.1"),sQuery(id+"F17.wireOp",EDGE,"E134.6.0.0"),sQuery(id+"F17.wireOp",EDGE,"E134.6.0.1"),sQuery(id+"F17.wireOp",EDGE,"E134.7.0.0"),sQuery(id+"F17.wireOp",EDGE,"E134.7.0.1"),sQuery(id+"F17.wireOp",EDGE,"E134.8.0.0"),sQuery(id+"F17.wireOp",EDGE,"E134.8.0.1"),sQuery(id+"F17.wireOp",EDGE,"E134.9.0.0"),sQuery(id+"F17.wireOp",EDGE,"E134.9.0.1"),sQuery(id+"F17.wireOp",EDGE,"E134.10.0.0"),sQuery(id+"F17.wireOp",EDGE,"E134.10.0.1"),sQuery(id+"F17.wireOp",EDGE,"E134.11.0.0"),sQuery(id+"F17.wireOp",EDGE,"E134.11.0.1"),sQuery(id+"F17.wireOp",EDGE,"E134.12.0.0"),sQuery(id+"F17.wireOp",EDGE,"E134.12.0.1"),sQuery(id+"F17.wireOp",EDGE,"E134.13.0.0"),sQuery(id+"F17.wireOp",EDGE,"E134.13.0.1"),sQuery(id+"F17.wireOp",EDGE,"E134.14.0.0"),sQuery(id+"F17.wireOp",EDGE,"E134.14.0.1"),sQuery(id+"F17.wireOp",EDGE,"E134.15.0.0"),sQuery(id+"F17.wireOp",EDGE,"E134.15.0.1"),sQuery(id+"F17.wireOp",EDGE,"E134.16.0.0"),sQuery(id+"F17.wireOp",EDGE,"E134.16.0.1"),sQuery(id+"F17.wireOp",EDGE,"E134.17.0.0"),sQuery(id+"F17.wireOp",EDGE,"E134.17.0.1"),sQuery(id+"F17.wireOp",EDGE,"E134.18.0.0"),sQuery(id+"F17.wireOp",EDGE,"E134.18.0.1"),sQuery(id+"F17.wireOp",EDGE,"E134.19.0.0"),sQuery(id+"F17.wireOp",EDGE,"E134.19.0.1"),sQuery(id+"F17.wireOp",EDGE,"E135"),sQuery(id+"F17.wireOp",EDGE,"E136"),sQuery(id+"F17.wireOp",EDGE,"E137"),sQuery(id+"F17.wireOp",EDGE,"E138")])]});
            var Q1;
            Q1=qCreatedBy(makeId("Front.planeOp"),FACE);
            mirror(context, id + "F19", {"entities" : qUnion([Q0]), "mirrorPlane" : qUnion([Q1])});
        }
        {
            var Q0;
            Q0=makeQuery(id+"F19.opPattern","COPY",BODY,{"derivedFrom":makeQuery(id+"F18.opExtrude","SWEPT_BODY",BODY,{"disambiguationData":[OSD([sQuery(id+"F17.wireOp",EDGE,"E132"),sQuery(id+"F17.wireOp",EDGE,"E133"),sQuery(id+"F17.wireOp",EDGE,"E134.1.0.0"),sQuery(id+"F17.wireOp",EDGE,"E134.1.0.1"),sQuery(id+"F17.wireOp",EDGE,"E134.2.0.0"),sQuery(id+"F17.wireOp",EDGE,"E134.2.0.1"),sQuery(id+"F17.wireOp",EDGE,"E134.3.0.0"),sQuery(id+"F17.wireOp",EDGE,"E134.3.0.1"),sQuery(id+"F17.wireOp",EDGE,"E134.4.0.0"),sQuery(id+"F17.wireOp",EDGE,"E134.4.0.1"),sQuery(id+"F17.wireOp",EDGE,"E134.5.0.0"),sQuery(id+"F17.wireOp",EDGE,"E134.5.0.1"),sQuery(id+"F17.wireOp",EDGE,"E134.6.0.0"),sQuery(id+"F17.wireOp",EDGE,"E134.6.0.1"),sQuery(id+"F17.wireOp",EDGE,"E134.7.0.0"),sQuery(id+"F17.wireOp",EDGE,"E134.7.0.1"),sQuery(id+"F17.wireOp",EDGE,"E134.8.0.0"),sQuery(id+"F17.wireOp",EDGE,"E134.8.0.1"),sQuery(id+"F17.wireOp",EDGE,"E134.9.0.0"),sQuery(id+"F17.wireOp",EDGE,"E134.9.0.1"),sQuery(id+"F17.wireOp",EDGE,"E134.10.0.0"),sQuery(id+"F17.wireOp",EDGE,"E134.10.0.1"),sQuery(id+"F17.wireOp",EDGE,"E134.11.0.0"),sQuery(id+"F17.wireOp",EDGE,"E134.11.0.1"),sQuery(id+"F17.wireOp",EDGE,"E134.12.0.0"),sQuery(id+"F17.wireOp",EDGE,"E134.12.0.1"),sQuery(id+"F17.wireOp",EDGE,"E134.13.0.0"),sQuery(id+"F17.wireOp",EDGE,"E134.13.0.1"),sQuery(id+"F17.wireOp",EDGE,"E134.14.0.0"),sQuery(id+"F17.wireOp",EDGE,"E134.14.0.1"),sQuery(id+"F17.wireOp",EDGE,"E134.15.0.0"),sQuery(id+"F17.wireOp",EDGE,"E134.15.0.1"),sQuery(id+"F17.wireOp",EDGE,"E134.16.0.0"),sQuery(id+"F17.wireOp",EDGE,"E134.16.0.1"),sQuery(id+"F17.wireOp",EDGE,"E134.17.0.0"),sQuery(id+"F17.wireOp",EDGE,"E134.17.0.1"),sQuery(id+"F17.wireOp",EDGE,"E134.18.0.0"),sQuery(id+"F17.wireOp",EDGE,"E134.18.0.1"),sQuery(id+"F17.wireOp",EDGE,"E134.19.0.0"),sQuery(id+"F17.wireOp",EDGE,"E134.19.0.1"),sQuery(id+"F17.wireOp",EDGE,"E135"),sQuery(id+"F17.wireOp",EDGE,"E136"),sQuery(id+"F17.wireOp",EDGE,"E137"),sQuery(id+"F17.wireOp",EDGE,"E138")])]}),"instanceName":"1"});
            var Q1;
            Q1=makeQuery(id+"F18.opExtrude","SWEPT_BODY",BODY,{"disambiguationData":[OSD([sQuery(id+"F17.wireOp",EDGE,"E132"),sQuery(id+"F17.wireOp",EDGE,"E133"),sQuery(id+"F17.wireOp",EDGE,"E134.1.0.0"),sQuery(id+"F17.wireOp",EDGE,"E134.1.0.1"),sQuery(id+"F17.wireOp",EDGE,"E134.2.0.0"),sQuery(id+"F17.wireOp",EDGE,"E134.2.0.1"),sQuery(id+"F17.wireOp",EDGE,"E134.3.0.0"),sQuery(id+"F17.wireOp",EDGE,"E134.3.0.1"),sQuery(id+"F17.wireOp",EDGE,"E134.4.0.0"),sQuery(id+"F17.wireOp",EDGE,"E134.4.0.1"),sQuery(id+"F17.wireOp",EDGE,"E134.5.0.0"),sQuery(id+"F17.wireOp",EDGE,"E134.5.0.1"),sQuery(id+"F17.wireOp",EDGE,"E134.6.0.0"),sQuery(id+"F17.wireOp",EDGE,"E134.6.0.1"),sQuery(id+"F17.wireOp",EDGE,"E134.7.0.0"),sQuery(id+"F17.wireOp",EDGE,"E134.7.0.1"),sQuery(id+"F17.wireOp",EDGE,"E134.8.0.0"),sQuery(id+"F17.wireOp",EDGE,"E134.8.0.1"),sQuery(id+"F17.wireOp",EDGE,"E134.9.0.0"),sQuery(id+"F17.wireOp",EDGE,"E134.9.0.1"),sQuery(id+"F17.wireOp",EDGE,"E134.10.0.0"),sQuery(id+"F17.wireOp",EDGE,"E134.10.0.1"),sQuery(id+"F17.wireOp",EDGE,"E134.11.0.0"),sQuery(id+"F17.wireOp",EDGE,"E134.11.0.1"),sQuery(id+"F17.wireOp",EDGE,"E134.12.0.0"),sQuery(id+"F17.wireOp",EDGE,"E134.12.0.1"),sQuery(id+"F17.wireOp",EDGE,"E134.13.0.0"),sQuery(id+"F17.wireOp",EDGE,"E134.13.0.1"),sQuery(id+"F17.wireOp",EDGE,"E134.14.0.0"),sQuery(id+"F17.wireOp",EDGE,"E134.14.0.1"),sQuery(id+"F17.wireOp",EDGE,"E134.15.0.0"),sQuery(id+"F17.wireOp",EDGE,"E134.15.0.1"),sQuery(id+"F17.wireOp",EDGE,"E134.16.0.0"),sQuery(id+"F17.wireOp",EDGE,"E134.16.0.1"),sQuery(id+"F17.wireOp",EDGE,"E134.17.0.0"),sQuery(id+"F17.wireOp",EDGE,"E134.17.0.1"),sQuery(id+"F17.wireOp",EDGE,"E134.18.0.0"),sQuery(id+"F17.wireOp",EDGE,"E134.18.0.1"),sQuery(id+"F17.wireOp",EDGE,"E134.19.0.0"),sQuery(id+"F17.wireOp",EDGE,"E134.19.0.1"),sQuery(id+"F17.wireOp",EDGE,"E135"),sQuery(id+"F17.wireOp",EDGE,"E136"),sQuery(id+"F17.wireOp",EDGE,"E137"),sQuery(id+"F17.wireOp",EDGE,"E138")])]});
            var Q2;
            Q2=qCreatedBy(makeId("Right.planeOp"),FACE);
            mirror(context, id + "F20", {"entities" : qUnion([Q0, Q1]), "mirrorPlane" : qUnion([Q2])});
        }
        {
            var Q0;
            Q0=makeQuery(id+"F11.opExtrude","CAP_FACE",FACE,{"disambiguationData":[OSD([sQuery(id+"F10.wireOp",EDGE,"E56.bottom"),sQuery(id+"F10.wireOp",EDGE,"E56.top"),sQuery(id+"F10.wireOp",EDGE,"E56.left"),sQuery(id+"F10.wireOp",EDGE,"E56.right"),sQuery(id+"F10.wireOp",EDGE,"E59.top"),sQuery(id+"F10.wireOp",EDGE,"E61"),sQuery(id+"F10.wireOp",EDGE,"E62"),sQuery(id+"F10.wireOp",EDGE,"E63"),sQuery(id+"F10.wireOp",EDGE,"E73.filletArc"),sQuery(id+"F10.wireOp",EDGE,"E74.filletArc"),sQuery(id+"F10.wireOp",EDGE,"E75.filletArc"),sQuery(id+"F10.wireOp",EDGE,"E76.filletArc")])],"isStart":false});
            var Q1;
            Q1=makeQuery(id+"F13.opExtrude","CAP_FACE",FACE,{"disambiguationData":[OSD([sQuery(id+"F12.wireOp",EDGE,"E78.bottom"),sQuery(id+"F12.wireOp",EDGE,"E78.top"),sQuery(id+"F12.wireOp",EDGE,"E78.left"),sQuery(id+"F12.wireOp",EDGE,"E78.right"),sQuery(id+"F12.wireOp",EDGE,"E81.top"),sQuery(id+"F12.wireOp",EDGE,"E83"),sQuery(id+"F12.wireOp",EDGE,"E84"),sQuery(id+"F12.wireOp",EDGE,"E85"),sQuery(id+"F12.wireOp",EDGE,"E95.filletArc"),sQuery(id+"F12.wireOp",EDGE,"E96.filletArc"),sQuery(id+"F12.wireOp",EDGE,"E97.filletArc"),sQuery(id+"F12.wireOp",EDGE,"E98.filletArc")])],"isStart":false});
            var Q2;
            Q2=makeQuery(id+"F14.opBoolean","MERGE",EDGE,{"derivedFrom":[makeQuery(id+"F9.opExtrude","SWEPT_EDGE",EDGE,{"disambiguationData":[OSD([sQuery(id+"F8.wireOp",EDGE,"E28.right"),sQuery(id+"F8.wireOp",EDGE,"E34")])]}),makeQuery(id+"F11.opExtrude","SWEPT_EDGE",EDGE,{"disambiguationData":[OSD([sQuery(id+"F10.wireOp",EDGE,"E56.bottom"),sQuery(id+"F10.wireOp",EDGE,"E56.left")])]})]});
            var Q3;
            Q3=makeQuery(id+"F13.opExtrude","SWEPT_EDGE",EDGE,{"disambiguationData":[OSD([sQuery(id+"F12.wireOp",EDGE,"E78.right"),sQuery(id+"F12.wireOp",EDGE,"E84")])]});
            var Q4;
            Q4=makeQuery(id+"F14.opBoolean","MERGE",EDGE,{"derivedFrom":[makeQuery(id+"F9.opExtrude","SWEPT_EDGE",EDGE,{"disambiguationData":[OSD([sQuery(id+"F8.wireOp",EDGE,"E28.top"),sQuery(id+"F8.wireOp",EDGE,"E28.right")])]}),makeQuery(id+"F11.opExtrude","SWEPT_EDGE",EDGE,{"disambiguationData":[OSD([sQuery(id+"F10.wireOp",EDGE,"E56.top"),sQuery(id+"F10.wireOp",EDGE,"E56.left")])]})]});
            var Q5;
            Q5=makeQuery(id+"F13.opExtrude","SWEPT_EDGE",EDGE,{"disambiguationData":[OSD([sQuery(id+"F12.wireOp",EDGE,"E78.top"),sQuery(id+"F12.wireOp",EDGE,"E78.right")])]});
            var Q6;
            Q6=makeQuery(id+"F14.opBoolean","MERGE",EDGE,{"derivedFrom":[makeQuery(id+"F9.opExtrude","SWEPT_EDGE",EDGE,{"disambiguationData":[OSD([sQuery(id+"F8.wireOp",EDGE,"E28.top"),sQuery(id+"F8.wireOp",EDGE,"E28.left")])]}),makeQuery(id+"F11.opExtrude","SWEPT_EDGE",EDGE,{"disambiguationData":[OSD([sQuery(id+"F10.wireOp",EDGE,"E56.top"),sQuery(id+"F10.wireOp",EDGE,"E56.right")])]})]});
            var Q7;
            Q7=makeQuery(id+"F13.opExtrude","SWEPT_EDGE",EDGE,{"disambiguationData":[OSD([sQuery(id+"F12.wireOp",EDGE,"E78.top"),sQuery(id+"F12.wireOp",EDGE,"E78.left")])]});
            var Q8;
            Q8=makeQuery(id+"F14.opBoolean","MERGE",EDGE,{"derivedFrom":[makeQuery(id+"F9.opExtrude","SWEPT_EDGE",EDGE,{"disambiguationData":[OSD([sQuery(id+"F8.wireOp",EDGE,"E28.bottom"),sQuery(id+"F8.wireOp",EDGE,"E28.left")])]}),makeQuery(id+"F11.opExtrude","SWEPT_EDGE",EDGE,{"disambiguationData":[OSD([sQuery(id+"F10.wireOp",EDGE,"E56.right"),sQuery(id+"F10.wireOp",EDGE,"E62")])]})]});
            var Q9;
            Q9=makeQuery(id+"F13.opExtrude","SWEPT_EDGE",EDGE,{"disambiguationData":[OSD([sQuery(id+"F12.wireOp",EDGE,"E78.bottom"),sQuery(id+"F12.wireOp",EDGE,"E78.left")])]});
            fillet(context, id + "F21", {"entities" : qUnion([Q0, Q1, Q2, Q3, Q4, Q5, Q6, Q7, Q8, Q9]), "radius" : 1 * mm, "tangentPropagation" : true, "allowEdgeOverflow" : false});
        }
    });
